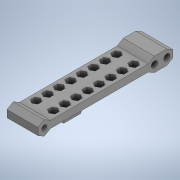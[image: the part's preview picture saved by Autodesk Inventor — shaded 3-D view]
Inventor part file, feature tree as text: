
AUTODESK INVENTOR PART (.ipt)
format: ipt  version: 2020 (Build 240168000, 168)  size: 462,848 bytes
history: native  units: in
note: dims shown in document units (in); Inventor stores cm internally (conversion verified against a paired STEP export)
features: sketch x7, extrude x6, projected_geometry x4, plane x2, mirror x1
ambient origin geometry x8: Origin, YZ Plane, XZ Plane, XY Plane, X Axis, Y Axis, Z Axis, Center Point
bodies: Solid1 (feature_tree)
feature tree (20):
  extrude  "Extrusion1"  Depth=3.4256in
  plane  "Work Plane1"
  extrude  "Extrusion2"  Depth=0.7874in
  sketch  "Sketch4"  dims[d4=0.0in d5=0.0827in]
  extrude  "Extrusion4"  Depth=0.0827in
  plane  "Work Plane2"
  extrude  "Extrusion6"  Depth=3.1106in
  mirror  "Mirror2"
  extrude  "Extrusion7"  Depth=0.315in
  extrude  "Extrusion8"  Depth=0.2362in
  sketch  "Sketch1"  dims[d0=0.1818in d1=3.4256in]
  sketch  "Sketch2"  dims[d2=0.1339in d3=0.7874in]
  sketch  "Sketch5"  dims[d6=0.7874in d7=0.0in d28=3.1106in]
  sketch  "Sketch7"  dims[d29=0.315in d31=0.315in]
  projected_geometry  "Projected Loop7"
  projected_geometry  "Projected Loop8"
  sketch  "Sketch8"  dims[d33=0.1575in d34=0.2362in]
  projected_geometry  "Projected Loop9"
  sketch  "Sketch10"  dims[d35=0.0in d38=0.315in d39=0.2756in d40=-0.3092in d41=0.0787in d42=0.0787in d43=0.0787in d44=3.1496in d46=0.2913in d47=0.3937in d49=0.3937in d51=3.1496in d53=0.2913in d54=0.3937in d56=0.3937in d58=0.0in d59=0.0in d60=150.0deg d61=0.1339in d63=1.1811in d64=0.1575in d65=0.0in d66=0.1181in]
  projected_geometry  "Projected Loop10"
